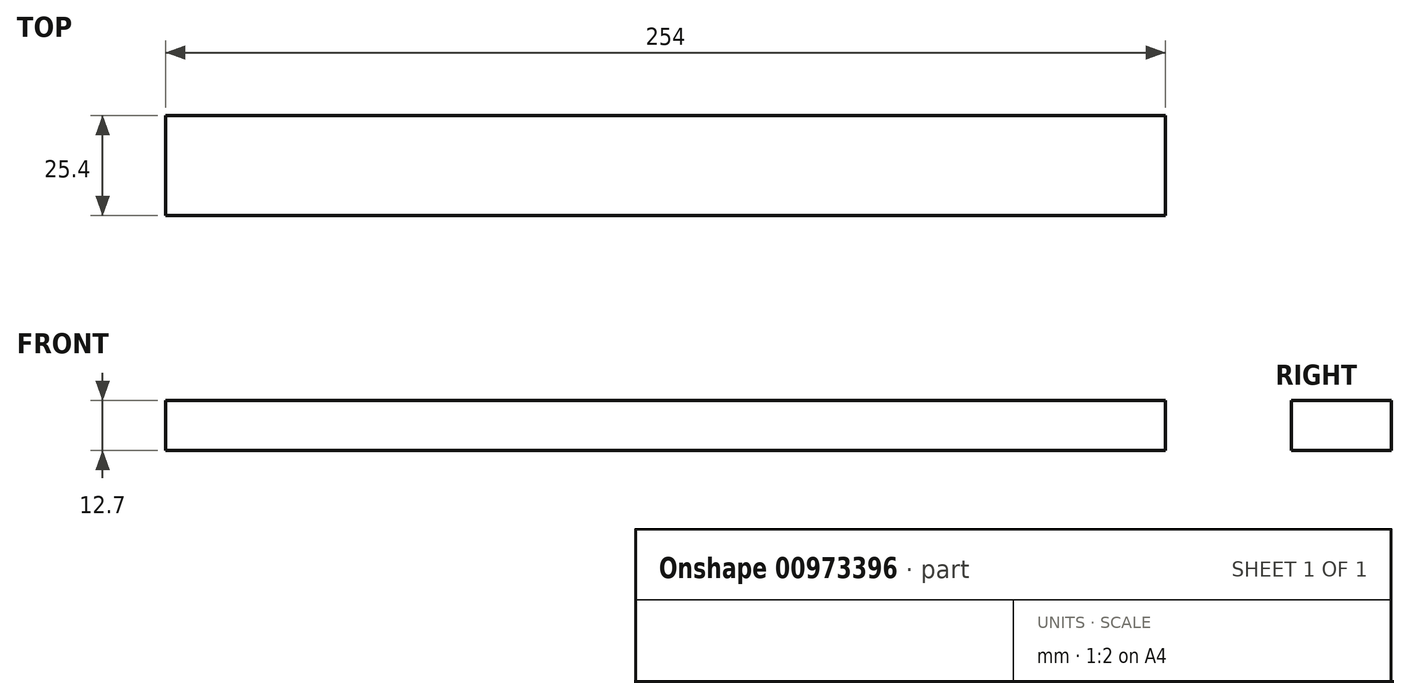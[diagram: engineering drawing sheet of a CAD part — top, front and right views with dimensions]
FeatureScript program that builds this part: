
annotation { "Feature Type Name" : "Feature", "Feature Type Description" : "" }
export const myFeature = defineFeature(function(context is Context, id is Id, definition is map)
    precondition{}
    {
        {
            var Q0;
            Q0=qCreatedBy(makeId("Front.planeOp"),FACE);
            var sketch = newSketch(context, id + "F0", { "sketchPlane" : qUnion([Q0])});
            skLineSegment(sketch, "E0.bottom", {"start": v(-162.96, 127.52) * mm, "end": v(91.04, 127.52) * mm});
            skLineSegment(sketch, "E0.top", {"start": v(-162.96, -126.48) * mm, "end": v(91.04, -126.48) * mm});
            skLineSegment(sketch, "E0.left", {"start": v(-162.96, 127.52) * mm, "end": v(-162.96, -126.48) * mm});
            skLineSegment(sketch, "E0.right", {"start": v(91.04, 127.52) * mm, "end": v(91.04, -126.48) * mm});
            skSolve(sketch);
        }
        {
            var Q0;
            Q0=qCreatedBy(makeId("Front.planeOp"),FACE);
            var sketch = newSketch(context, id + "F1", { "sketchPlane" : qUnion([Q0])});
            skLineSegment(sketch, "E1.bottom", {"start": v(91.04, 127.52) * mm, "end": v(-162.96, 127.52) * mm});
            skLineSegment(sketch, "E1.top", {"start": v(91.04, 114.82) * mm, "end": v(-162.96, 114.82) * mm});
            skLineSegment(sketch, "E1.left", {"start": v(91.04, 127.52) * mm, "end": v(91.04, 114.82) * mm});
            skLineSegment(sketch, "E1.right", {"start": v(-162.96, 127.52) * mm, "end": v(-162.96, 114.82) * mm});
            skSolve(sketch);
        }
        {
            var Q0;
            Q0 = qSketchRegion(id + "F1", true);
            extrude(context, id + "F2", {"entities" : qUnion([Q0]), "depth" : 25.4 * mm, "offsetDistance" : 25.4 * mm});
        }
    });
